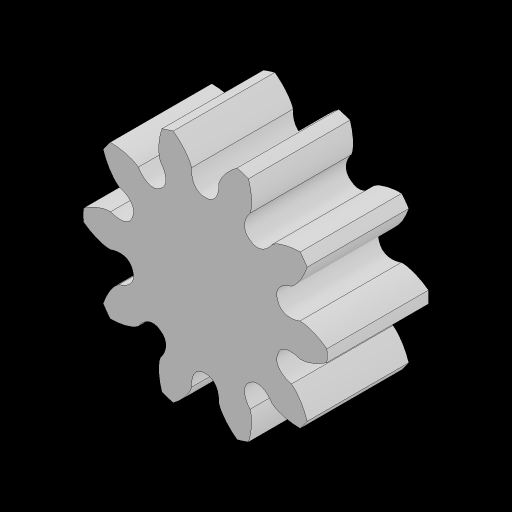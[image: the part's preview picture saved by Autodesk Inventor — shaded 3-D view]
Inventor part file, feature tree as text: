
AUTODESK INVENTOR PART (.ipt)
format: ipt  version: 2023.2 (Build 272271030, 271C)  size: 208,384 bytes
history: native  units: mm
features: extrude x2, sketch x1, pattern_circular x1
ambient origin geometry x8: Origin, YZ Plane, XZ Plane, XY Plane, X Axis, Y Axis, Z Axis, Center Point
bodies: Solid1 (feature_tree)
feature tree (4):
  sketch  "Sketch1"  dims[d0=5.0mm d1=0.0mm d2=0.0mm d3=0.0mm d4=100.0mm d5=360.0deg]
  extrude  "Extrusion1"  TaperAngle=0.0deg  [1 undecoded]
  extrude  "Extrusion2"  Depth=100.0mm TaperAngle=360.0deg
  pattern_circular  "Circular Pattern1"  [2 undecoded]
note: 3 required parameter values undecoded (feature->parameter linkage not recoverable at this tier; creation-order binding heuristic only, values carry confidence <= 0.55)
